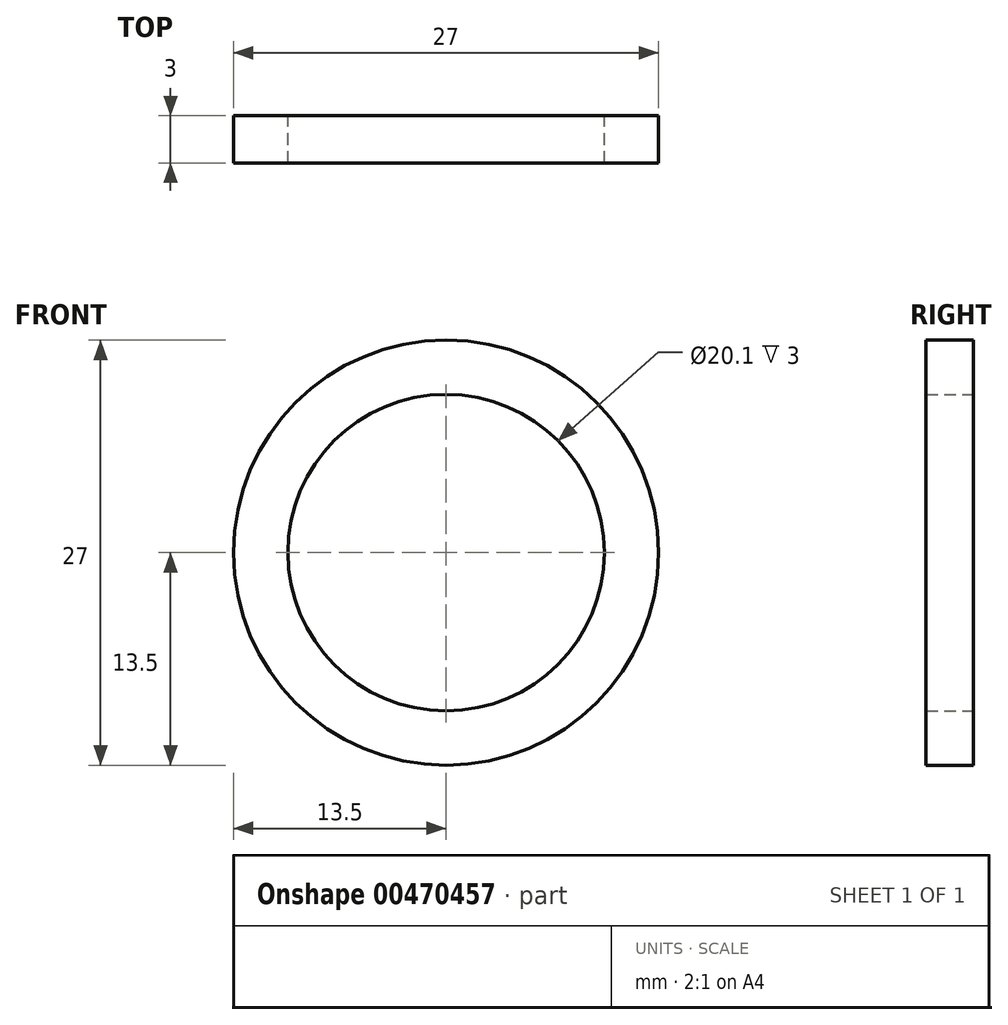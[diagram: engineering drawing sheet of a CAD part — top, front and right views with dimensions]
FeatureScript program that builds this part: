
annotation { "Feature Type Name" : "Feature", "Feature Type Description" : "" }
export const myFeature = defineFeature(function(context is Context, id is Id, definition is map)
    precondition{}
    {
        {
            var Q0;
            Q0=qCreatedBy(makeId("Front.planeOp"),FACE);
            var sketch = newSketch(context, id + "F0", { "sketchPlane" : qUnion([Q0])});
            skCircle(sketch, "E0", {"center": v(0, 0) * mm, "radius": 13.5 * mm});
            skCircle(sketch, "E1", {"center": v(0, 0) * mm, "radius": 10.05 * mm});
            skSolve(sketch);
        }
        {
            var Q0;
            Q0=makeQuery(id+"F0.imprint","IMPRINT",FACE,{"disambiguationData":[TD([[makeQuery(id+"F0.imprint","IMPRINT",EDGE,{"derivedFrom":sQuery(id+"F0.wireOp",EDGE,"E0")}),1.0]])]});
            extrude(context, id + "F1", {"entities" : qUnion([Q0]), "endBound" : BoundingType.SYMMETRIC, "depth" : 3 * mm});
        }
    });
